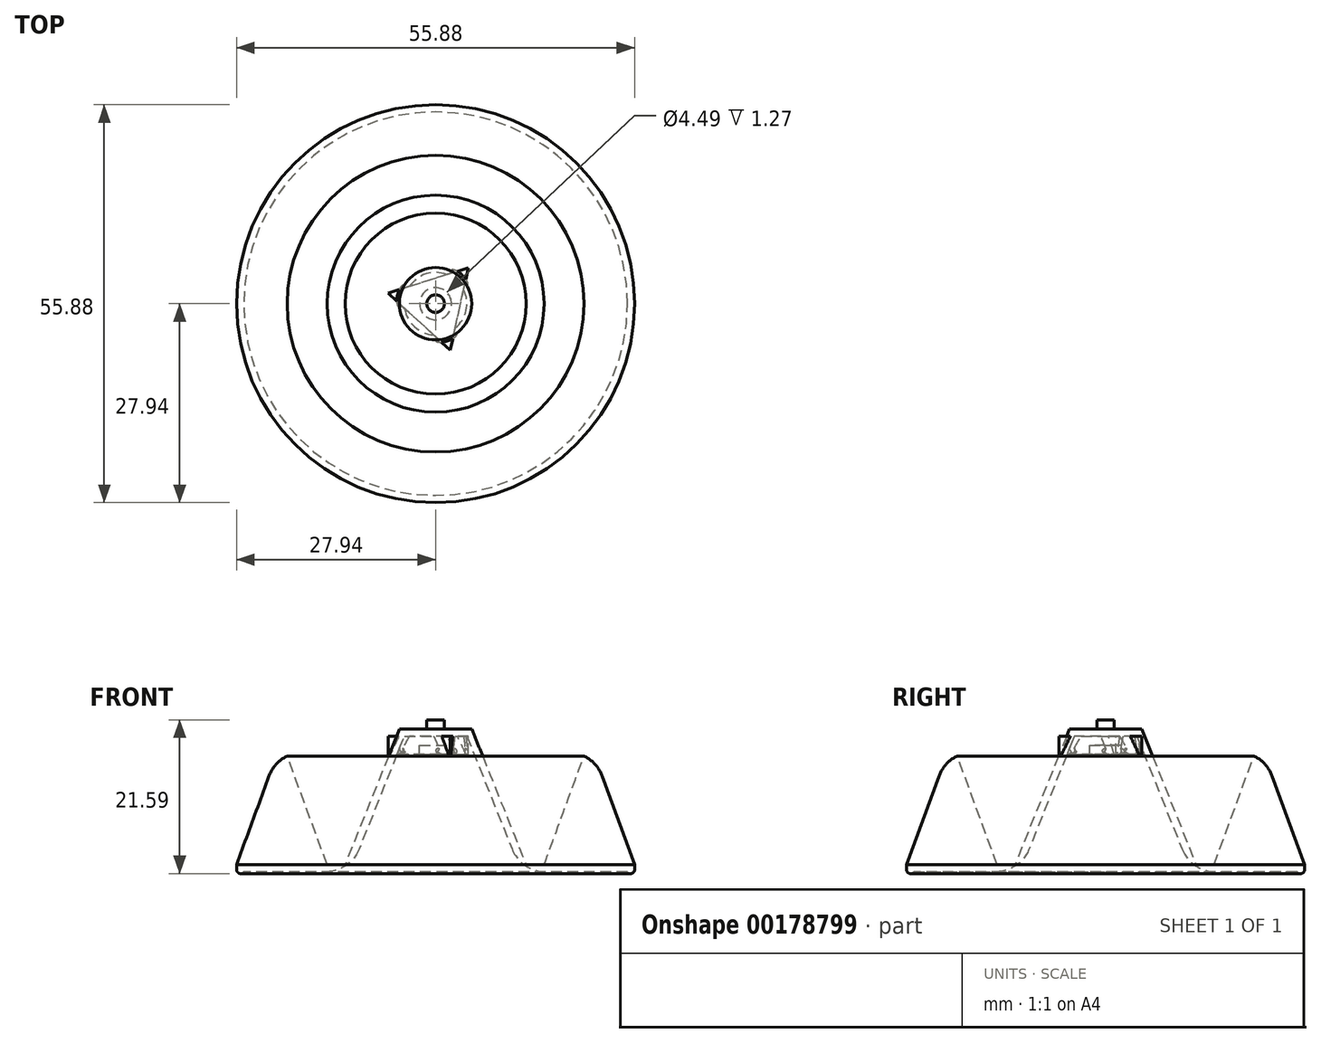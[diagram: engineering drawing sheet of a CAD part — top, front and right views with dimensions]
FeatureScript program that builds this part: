
annotation { "Feature Type Name" : "Feature", "Feature Type Description" : "" }
export const myFeature = defineFeature(function(context is Context, id is Id, definition is map)
    precondition{}
    {
        {
            var Q0;
            Q0=qCreatedBy(makeId("Top.planeOp"),FACE);
            var sketch = newSketch(context, id + "F0", { "sketchPlane" : qUnion([Q0])});
            skCircle(sketch, "E0", {"center": v(0, 0) * mm, "radius": 27.94 * mm});
            skSolve(sketch);
        }
        {
            var Q0;
            Q0=makeQuery(id+"F0.imprint","IMPRINT",FACE,{"disambiguationData":[TD([[makeQuery(id+"F0.imprint","IMPRINT",EDGE,{"derivedFrom":sQuery(id+"F0.wireOp",EDGE,"E0")}),1.0]])]});
            extrude(context, id + "F1", {"entities" : qUnion([Q0]), "depth" : 1.27 * mm});
        }
        {
            var Q0;
            Q0=makeQuery(id+"F1.opExtrude","CAP_FACE",FACE,{"disambiguationData":[OSD([sQuery(id+"F0.wireOp",EDGE,"E0")])],"isStart":false});
            var sketch = newSketch(context, id + "F2", { "sketchPlane" : qUnion([Q0])});
            skCircle(sketch, "E1", {"center": v(0, 0) * mm, "radius": 12.7 * mm});
            skSolve(sketch);
        }
        {
            var Q0;
            Q0=makeQuery(id+"F2.imprint","IMPRINT",FACE,{"disambiguationData":[TD([[makeQuery(id+"F2.imprint","IMPRINT",EDGE,{"derivedFrom":sQuery(id+"F2.wireOp",EDGE,"E1")}),1.0]])]});
            extrude(context, id + "F3", {"entities" : qUnion([Q0]), "operationType" : NewBodyOperationType.ADD, "depth" : 19.05 * mm});
        }
        {
            var Q0;
            Q0=makeQuery(id+"F3.opExtrude","CAP_FACE",FACE,{"disambiguationData":[OSD([sQuery(id+"F2.wireOp",EDGE,"E1")])],"isStart":false});
            chamfer(context, id + "F4", {"entities" : qUnion([Q0]), "chamferType" : ChamferType.TWO_OFFSETS, "width1" : 7.62 * mm, "oppositeDirection" : false, "width2" : 19.05 * mm, "tangentPropagation" : true});
        }
        {
            var Q0;
            Q0=makeQuery(id+"F1.opExtrude","CAP_FACE",FACE,{"disambiguationData":[OSD([sQuery(id+"F0.wireOp",EDGE,"E0")])],"isStart":false});
            var sketch = newSketch(context, id + "F5", { "sketchPlane" : qUnion([Q0])});
            skCircle(sketch, "E2", {"center": v(0, 0) * mm, "radius": 27.94 * mm});
            skCircle(sketch, "E3", {"center": v(0, 0) * mm, "radius": 15.24 * mm});
            skSolve(sketch);
        }
        {
            var Q0;
            Q0=makeQuery(id+"F1.opExtrude","CAP_FACE",FACE,{"disambiguationData":[OSD([sQuery(id+"F0.wireOp",EDGE,"E0")])],"isStart":true});
            shell(context, id + "F6", {"entities" : qUnion([Q0]), "thickness" : 1.02 * mm});
        }
        {
            var Q0;
            Q0 = qSketchRegion(id + "F5", true);
            extrude(context, id + "F7", {"entities" : qUnion([Q0]), "operationType" : NewBodyOperationType.ADD, "depth" : 15.24 * mm});
        }
        {
            var Q0;
            Q0=makeQuery(id+"F7.opExtrude","CAP_FACE",FACE,{"disambiguationData":[OSD([sQuery(id+"F5.wireOp",EDGE,"E2"),sQuery(id+"F5.wireOp",EDGE,"E3")])],"isStart":false});
            chamfer(context, id + "F8", {"entities" : qUnion([Q0]), "chamferType" : ChamferType.TWO_OFFSETS, "width1" : 5.6 * mm, "oppositeDirection" : false, "width2" : 15.24 * mm, "tangentPropagation" : true});
        }
        {
            var Q0;
            Q0=makeQuery(id+"F1.opExtrude","CAP_FACE",FACE,{"disambiguationData":[OSD([sQuery(id+"F0.wireOp",EDGE,"E0")])],"isStart":true});
            fillet(context, id + "F9", {"entities" : qUnion([Q0]), "radius" : 0.55 * mm, "tangentPropagation" : true, "allowEdgeOverflow" : false});
        }
        {
            var Q0;
            Q0=makeQuery(id+"F6.opShell","OFFSET_EDGE",EDGE,{"disambiguationData":[OSD([sQuery(id+"F0.wireOp",EDGE,"E0"),sQuery(id+"F2.wireOp",EDGE,"E1")])]});
            fillet(context, id + "F10", {"entities" : qUnion([Q0]), "radius" : 5.08 * mm, "tangentPropagation" : true, "allowEdgeOverflow" : false});
        }
        {
            var Q0;
            {var subQ0=sQuery(id+"F5.wireOp",EDGE,"E2");Q0=makeQuery(id+"F8.opChamfer","BLEND_EDGE",EDGE,{"blendedFrom":[makeQuery(id+"F7.opExtrude","CAP_EDGE",EDGE,{"disambiguationData":[OSD([subQ0])],"isStart":false}),makeQuery(id+"F7.opExtrude","CAP_FACE",FACE,{"disambiguationData":[OSD([subQ0,sQuery(id+"F5.wireOp",EDGE,"E3")])],"isStart":false})],"blendedInto":[makeQuery(id+"F7.opExtrude","CAP_FACE",FACE,{"disambiguationData":[OSD([subQ0,sQuery(id+"F5.wireOp",EDGE,"E3")])],"isStart":false})]});}
            fillet(context, id + "F11", {"entities" : qUnion([Q0]), "radius" : 5.08 * mm, "tangentPropagation" : true, "allowEdgeOverflow" : false});
        }
        {
            var Q0;
            {var subQ0=sQuery(id+"F2.wireOp",EDGE,"E1");Q0=makeQuery(id+"F6.opShell","OFFSET_FACE",FACE,{"disambiguationData":[OSD([subQ0]),TDD([makeQuery(id+"F3.opExtrude","CAP_FACE",FACE,{"disambiguationData":[OSD([subQ0])],"isStart":false})])]});}
            var sketch = newSketch(context, id + "F12", { "sketchPlane" : qUnion([Q0])});
            skCircle(sketch, "E4.cCircle", {"center": v(0, 0) * mm, "radius": 3.42 * mm, "construction": true});
            skLineSegment(sketch, "E4.0", {"start": v(-6.68, -1.47) * mm, "end": v(2.07, 6.52) * mm});
            skLineSegment(sketch, "E4.1", {"start": v(2.07, 6.52) * mm, "end": v(4.61, -5.05) * mm});
            skLineSegment(sketch, "E4.2", {"start": v(4.61, -5.05) * mm, "end": v(-6.68, -1.47) * mm});
            skPoint(sketch, "E4.0.midPoint", {"position": v(-2.3, 2.53) * mm});
            skSolve(sketch);
        }
        {
            var Q0;
            Q0 = qSketchRegion(id + "F12", true);
            extrude(context, id + "F13", {"entities" : qUnion([Q0]), "operationType" : NewBodyOperationType.ADD, "depth" : 2.54 * mm});
        }
        {
            var Q0;
            {var subQ0=sQuery(id+"F2.wireOp",EDGE,"E1");var subQ1=sQuery(id+"F12.wireOp",EDGE,"E4.0");var subQ2=sQuery(id+"F12.wireOp",EDGE,"E4.2");var subQ3=sQuery(id+"F12.wireOp",EDGE,"E4.1");Q0=makeQuery(id+"F13.boolean.opBoolean","SPLIT",FACE,{"disambiguationData":[TD([makeQuery(id+"F6.opShell","OFFSET_FACE",FACE,{"disambiguationData":[OSD([subQ0]),TDD([makeQuery(id+"F4.opChamfer","BLEND_FACE",FACE,{"disambiguationData":[OSD([subQ0])]})])]}),makeQuery(id+"F13.opExtrude","SWEPT_FACE",FACE,{"disambiguationData":[OSD([subQ1])]}),makeQuery(id+"F13.opExtrude","SWEPT_FACE",FACE,{"disambiguationData":[OSD([subQ3])]}),makeQuery(id+"F13.opExtrude","SWEPT_FACE",FACE,{"disambiguationData":[OSD([subQ2])]})])],"derivedFrom":makeQuery(id+"F13.opExtrude","CAP_FACE",FACE,{"disambiguationData":[OSD([subQ1,subQ3,subQ2])],"isStart":false})});}
            fillet(context, id + "F14", {"entities" : qUnion([Q0]), "radius" : 0.25 * mm, "tangentPropagation" : true, "allowEdgeOverflow" : false});
        }
        {
            var Q0;
            {var subQ0=sQuery(id+"F2.wireOp",EDGE,"E1");var subQ1=sQuery(id+"F12.wireOp",EDGE,"E4.0");var subQ2=sQuery(id+"F12.wireOp",EDGE,"E4.2");var subQ3=sQuery(id+"F12.wireOp",EDGE,"E4.1");Q0=makeQuery(id+"F13.boolean.opBoolean","SPLIT",FACE,{"disambiguationData":[TD([makeQuery(id+"F6.opShell","OFFSET_FACE",FACE,{"disambiguationData":[OSD([subQ0]),TDD([makeQuery(id+"F4.opChamfer","BLEND_FACE",FACE,{"disambiguationData":[OSD([subQ0])]})])]}),makeQuery(id+"F13.opExtrude","SWEPT_FACE",FACE,{"disambiguationData":[OSD([subQ1])]}),makeQuery(id+"F13.opExtrude","SWEPT_FACE",FACE,{"disambiguationData":[OSD([subQ3])]}),makeQuery(id+"F13.opExtrude","SWEPT_FACE",FACE,{"disambiguationData":[OSD([subQ2])]})])],"derivedFrom":makeQuery(id+"F13.opExtrude","CAP_FACE",FACE,{"disambiguationData":[OSD([subQ1,subQ3,subQ2])],"isStart":false})});}
            var sketch = newSketch(context, id + "F15", { "sketchPlane" : qUnion([Q0])});
            skCircle(sketch, "E5", {"center": v(0, 0) * mm, "radius": 1.51 * mm});
            skCircle(sketch, "E6", {"center": v(0, 0) * mm, "radius": 2.25 * mm});
            skSolve(sketch);
        }
        {
            var Q0;
            Q0=makeQuery(id+"F15.imprint","IMPRINT",FACE,{"disambiguationData":[TD([[makeQuery(id+"F15.imprint","IMPRINT",EDGE,{"derivedFrom":sQuery(id+"F15.wireOp",EDGE,"E5")}),-1.0]])]});
            extrude(context, id + "F16", {"entities" : qUnion([Q0]), "operationType" : NewBodyOperationType.REMOVE, "depth" : 2.54 * mm, "hasSecondDirection" : true, "secondDirectionOppositeDirection" : true, "secondDirectionDepth" : 1.27 * mm});
        }
        {
            var Q0;
            Q0=makeQuery(id+"F3.opExtrude","CAP_FACE",FACE,{"disambiguationData":[OSD([sQuery(id+"F2.wireOp",EDGE,"E1")])],"isStart":false});
            var sketch = newSketch(context, id + "F17", { "sketchPlane" : qUnion([Q0])});
            skCircle(sketch, "E7", {"center": v(0, 0) * mm, "radius": 1.23 * mm});
            skSolve(sketch);
        }
        {
            var Q0;
            Q0=makeQuery(id+"F17.imprint","IMPRINT",FACE,{"disambiguationData":[TD([[makeQuery(id+"F17.imprint","IMPRINT",EDGE,{"derivedFrom":sQuery(id+"F17.wireOp",EDGE,"E7")}),1.0]])]});
            extrude(context, id + "F18", {"entities" : qUnion([Q0]), "operationType" : NewBodyOperationType.ADD, "depth" : 1.27 * mm});
        }
        {
            var Q0;
            {var subQ0=sQuery(id+"F2.wireOp",EDGE,"E1");var subQ1=sQuery(id+"F12.wireOp",EDGE,"E4.0");var subQ2=sQuery(id+"F12.wireOp",EDGE,"E4.2");var subQ3=sQuery(id+"F12.wireOp",EDGE,"E4.1");Q0=makeQuery(id+"F16.boolean.opBoolean","SPLIT",FACE,{"disambiguationData":[TD([makeQuery(id+"F16.opExtrude","SWEPT_FACE",FACE,{"disambiguationData":[OSD([sQuery(id+"F15.wireOp",EDGE,"E5")])]})])],"derivedFrom":makeQuery(id+"F13.boolean.opBoolean","SPLIT",FACE,{"disambiguationData":[TD([makeQuery(id+"F6.opShell","OFFSET_FACE",FACE,{"disambiguationData":[OSD([subQ0]),TDD([makeQuery(id+"F4.opChamfer","BLEND_FACE",FACE,{"disambiguationData":[OSD([subQ0])]})])]}),makeQuery(id+"F13.opExtrude","SWEPT_FACE",FACE,{"disambiguationData":[OSD([subQ1])]}),makeQuery(id+"F13.opExtrude","SWEPT_FACE",FACE,{"disambiguationData":[OSD([subQ3])]}),makeQuery(id+"F13.opExtrude","SWEPT_FACE",FACE,{"disambiguationData":[OSD([subQ2])]})])],"derivedFrom":makeQuery(id+"F13.opExtrude","CAP_FACE",FACE,{"disambiguationData":[OSD([subQ1,subQ3,subQ2])],"isStart":false})})});}
            extrude(context, id + "F19", {"entities" : qUnion([Q0]), "operationType" : NewBodyOperationType.REMOVE, "oppositeDirection" : true, "depth" : 1.27 * mm});
        }
    });
